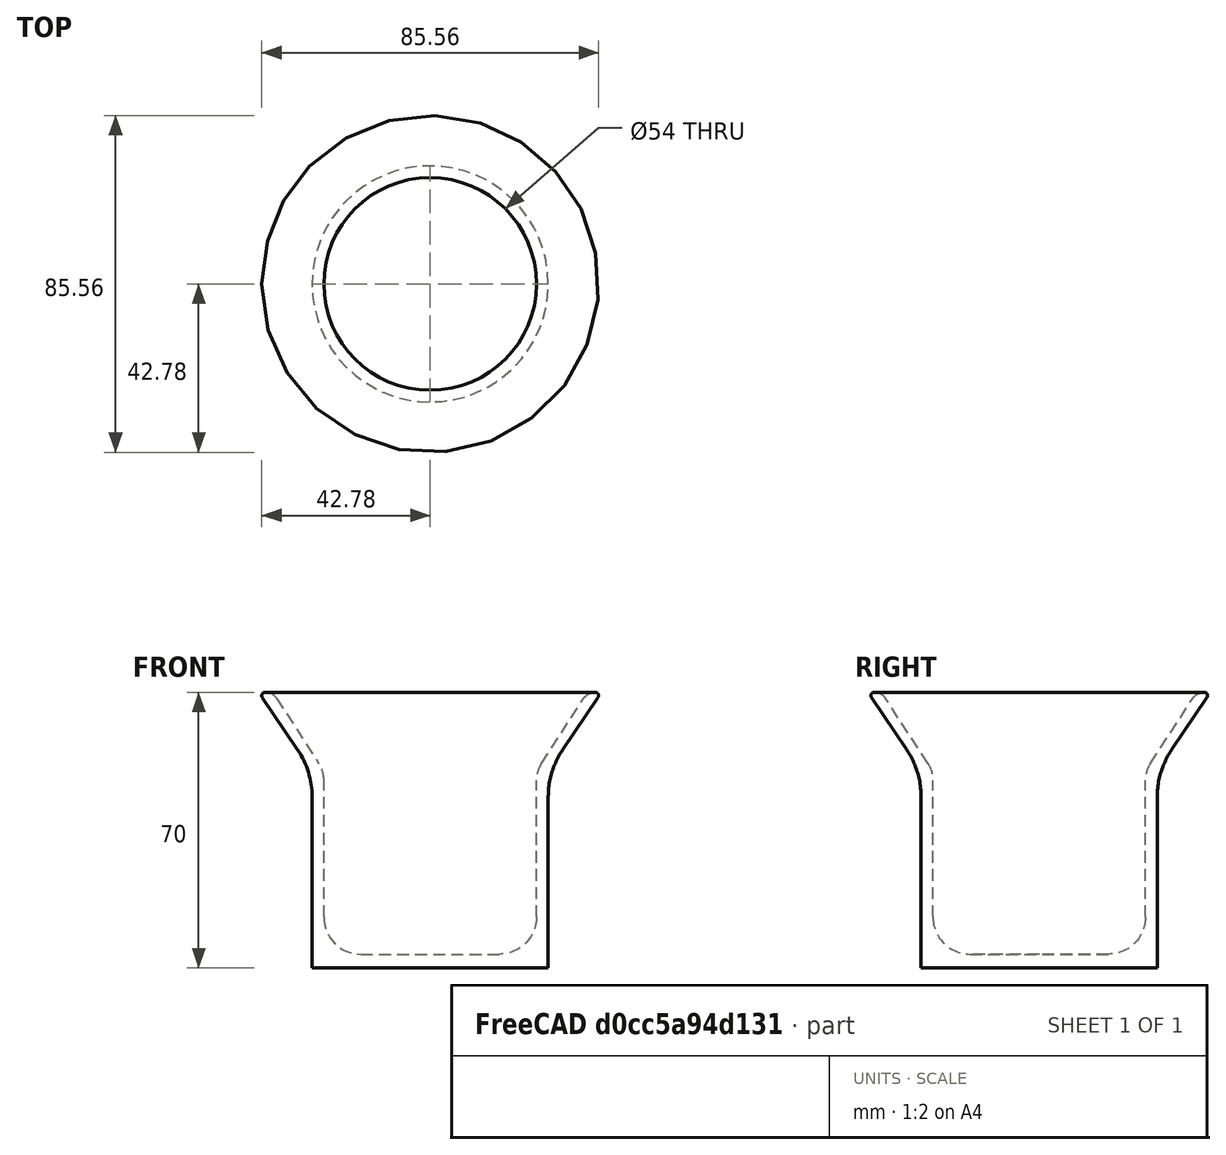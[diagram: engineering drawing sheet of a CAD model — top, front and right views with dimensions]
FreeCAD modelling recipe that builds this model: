
FCSTD DOCUMENT  (FreeCAD 1.1R40122 (Git))
Label: горшок для лука
License: All rights reserved
LicenseURL: https://en.wikipedia.org/wiki/All_rights_reserved
objects: App::Point×2, Sketcher::SketchObject×1, PartDesign::Revolution×1, PartDesign::Body×1, App::Part×1
note: 6 computed .brp shape members not serialized (recipe doc carries the construction recipe); baked Part::Feature solids carry a one-line shape summary decoded from their .brp

FEATURE [App::Point] Origin001  label="Начало координат"
  Role = Origin
FEATURE [App::Point] Origin003  label="Начало координат002"
  Role = Origin
FEATURE [Sketcher::SketchObject] Sketch
  ArcFitTolerance = 1e-06
  AttachmentSupport = -> [XZ_Plane001]
  ExternalTypes = [0]
  FullyConstrained = false
  MakeInternals = false
  MapMode = 5
  Placement = pos=(0,0,0) rot=(1,0,0;1.5708rad)
  sketch-geometry (18):
    g0: LineSegment StartX=0 StartY=0 StartZ=0 EndX=-30 EndY=0 EndZ=0
    g1: LineSegment StartX=0 StartY=0 StartZ=0 EndX=0 EndY=3.5 EndZ=0
    g2: LineSegment StartX=0 StartY=3.5 StartZ=0 EndX=-17.5894 EndY=3.5 EndZ=0
    g3: LineSegment StartX=-30 StartY=0 StartZ=0 EndX=-30 EndY=43.5187 EndZ=0
    g4: LineSegment StartX=-27 StartY=12.9106 StartZ=0 EndX=-27 EndY=47.6193 EndZ=0
    g5: LineSegment StartX=-33.6261 StartY=55.3721 StartZ=0 EndX=-42.6433 EndY=68.7309 EndZ=0
    g6: LineSegment StartX=-41.9688 StartY=70 StartZ=0 EndX=-41.8155 EndY=70 EndZ=0
    g7: LineSegment StartX=-39.0106 StartY=68.4778 StartZ=0 EndX=-28.2975 EndY=51.9961 EndZ=0
    g8: ArcOfCircle CenterX=-35.031 CenterY=47.6193 CenterZ=0 NormalX=0 NormalY=0 NormalZ=1 AngleXU=0 Radius=8.03098 StartAngle=0 EndAngle=0.576375
    g9: GeomPoint [constr] X=-27 Y=50 Z=0
    g10: ArcOfCircle CenterX=-51.1867 CenterY=43.5187 CenterZ=0 NormalX=0 NormalY=0 NormalZ=1 AngleXU=0 Radius=21.1867 StartAngle=0 EndAngle=0.59375
    g11: GeomPoint [constr] X=-30 Y=50 Z=0
    g12: ArcOfCircle CenterX=-41.9688 CenterY=69.1862 CenterZ=0 NormalX=0 NormalY=0 NormalZ=1 AngleXU=0 Radius=0.813829 StartAngle=1.5708 EndAngle=3.73534
    g13: GeomPoint [constr] X=-43.5 Y=70 Z=0
    g14: ArcOfCircle CenterX=-41.8155 CenterY=66.6545 CenterZ=0 NormalX=0 NormalY=0 NormalZ=1 AngleXU=0 Radius=3.34545 StartAngle=0.576375 EndAngle=1.5708
    g15: GeomPoint [constr] X=-40 Y=70 Z=0
    g16: ArcOfCircle CenterX=-17.5894 CenterY=12.9106 CenterZ=0 NormalX=0 NormalY=0 NormalZ=1 AngleXU=0 Radius=9.41057 StartAngle=3.14159 EndAngle=4.71239
    g17: GeomPoint [constr] X=-27 Y=3.5 Z=0
  constraints (38):
    c: Coincident(g0,g-1)
    c: PointOnObject(g0,g-1)
    c: DistanceX(g0,g0) = 30
    c: Coincident(g1,g0)
    c: PointOnObject(g1,g-2)
    c: Distance(g1,g1) = 3.5
    c: Coincident(g2,g1)
    c: Horizontal(g2)
    c: DistanceX(g17,g2) = 27
    c: Coincident(g3,g0)
    c: Vertical(g3)
    c: Vertical(g4)
    c: Horizontal(g6)
    c: Horizontal(g9,g11)
    c: DistanceY(g3,g11) = 50
    c: DistanceY(g-1,g13) = 70
    c: Distance(g13,g15) = 3.5
    c: Distance(g15,g-2) = 40
    c: PointOnObject(g9,g4)
    c: PointOnObject(g9,g7)
    c: Tangent(g4,g8) = -1.5708
    c: Tangent(g7,g8) = 1.5708
    c: PointOnObject(g11,g3)
    c: PointOnObject(g11,g5)
    c: Tangent(g3,g10) = -1.5708
    c: Tangent(g5,g10) = -1.5708
    c: PointOnObject(g13,g5)
    c: PointOnObject(g13,g6)
    c: Tangent(g5,g12) = 1.5708
    c: Tangent(g6,g12) = 1.5708
    c: PointOnObject(g15,g7)
    c: PointOnObject(g15,g6)
    c: Tangent(g7,g14) = 1.5708
    c: Tangent(g6,g14) = 1.5708
    c: PointOnObject(g17,g4)
    c: PointOnObject(g17,g2)
    c: Tangent(g4,g16) = 1.5708
    c: Tangent(g2,g16) = 1.5708
FEATURE [PartDesign::Revolution] Revolution
  Angle = 360
  Angle2 = 60
  Axis = (0,2e-16,1)
  Base = (0,0,0)
  Placement = pos=(0,0,0) rot=(1,0,0;1.5708rad)
  Profile = -> Sketch
  ReferenceAxis = -> Sketch [V_Axis]
  Refine = true
  Suppressed = false
  Type = 0
FEATURE [PartDesign::Body] Body
  AllowCompound = false
  Group = -> [Sketch,Revolution]
  Origin = -> Origin002
  Tip = -> Revolution
FEATURE [App::Part] Part
  Group = -> [Body]
  Origin = -> Origin
